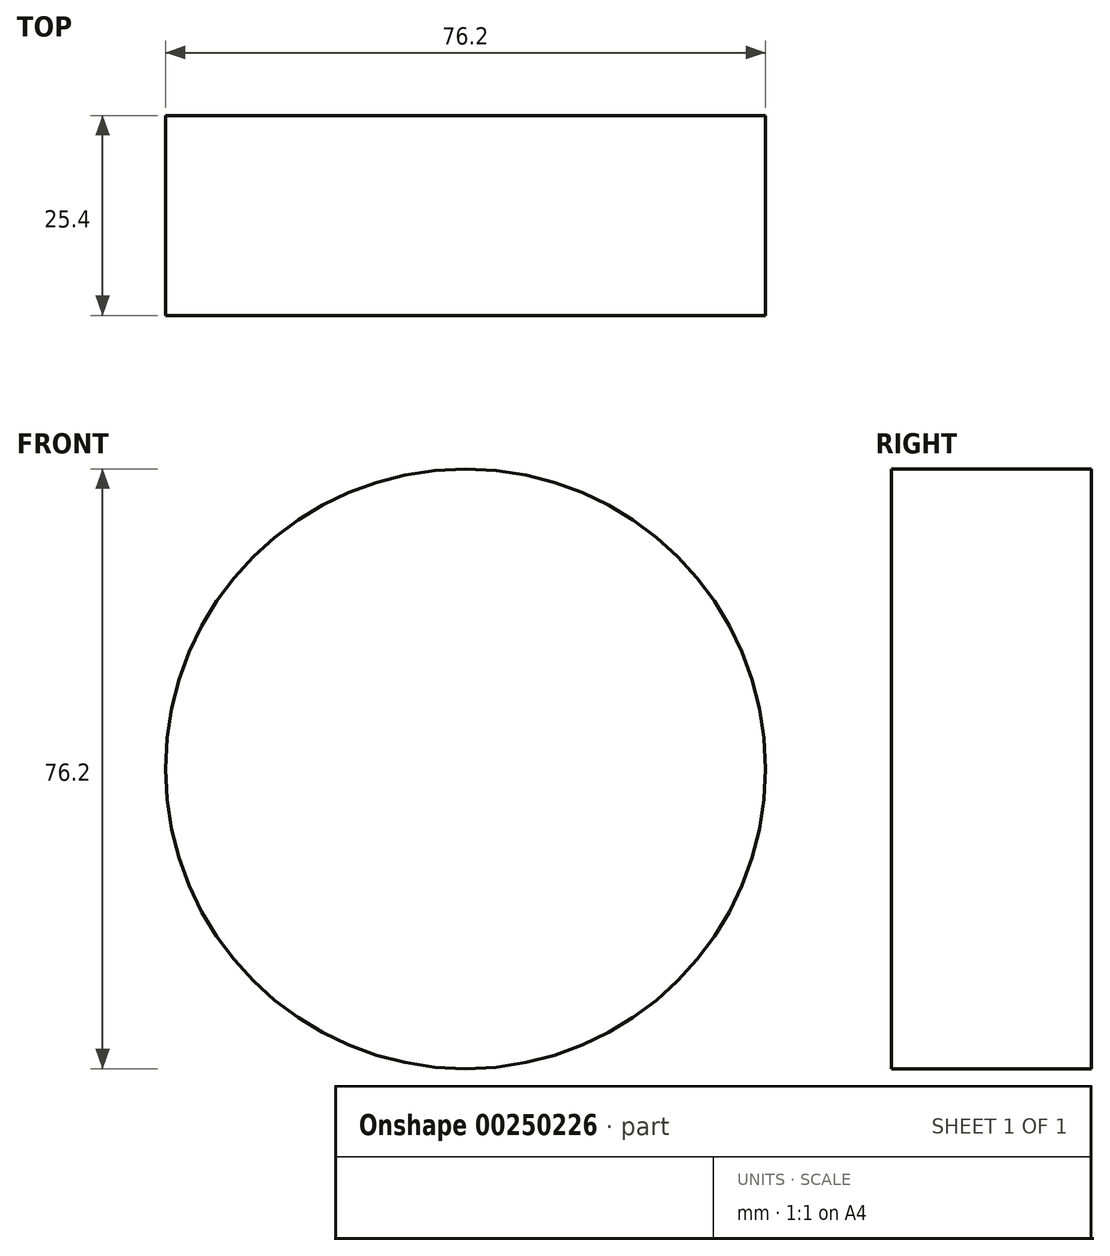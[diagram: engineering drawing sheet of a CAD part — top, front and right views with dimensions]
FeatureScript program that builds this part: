
annotation { "Feature Type Name" : "Feature", "Feature Type Description" : "" }
export const myFeature = defineFeature(function(context is Context, id is Id, definition is map)
    precondition{}
    {
        {
            var Q0;
            Q0=qCreatedBy(makeId("Front.planeOp"),FACE);
            var sketch = newSketch(context, id + "F0", { "sketchPlane" : qUnion([Q0])});
            skCircle(sketch, "E0", {"center": v(0, 0) * mm, "radius": 38.1 * mm});
            skSolve(sketch);
        }
        {
            var Q0;
            Q0 = qSketchRegion(id + "F0", true);
            extrude(context, id + "F1", {"entities" : qUnion([Q0]), "oppositeDirection" : true, "depth" : 25.4 * mm});
        }
    });
